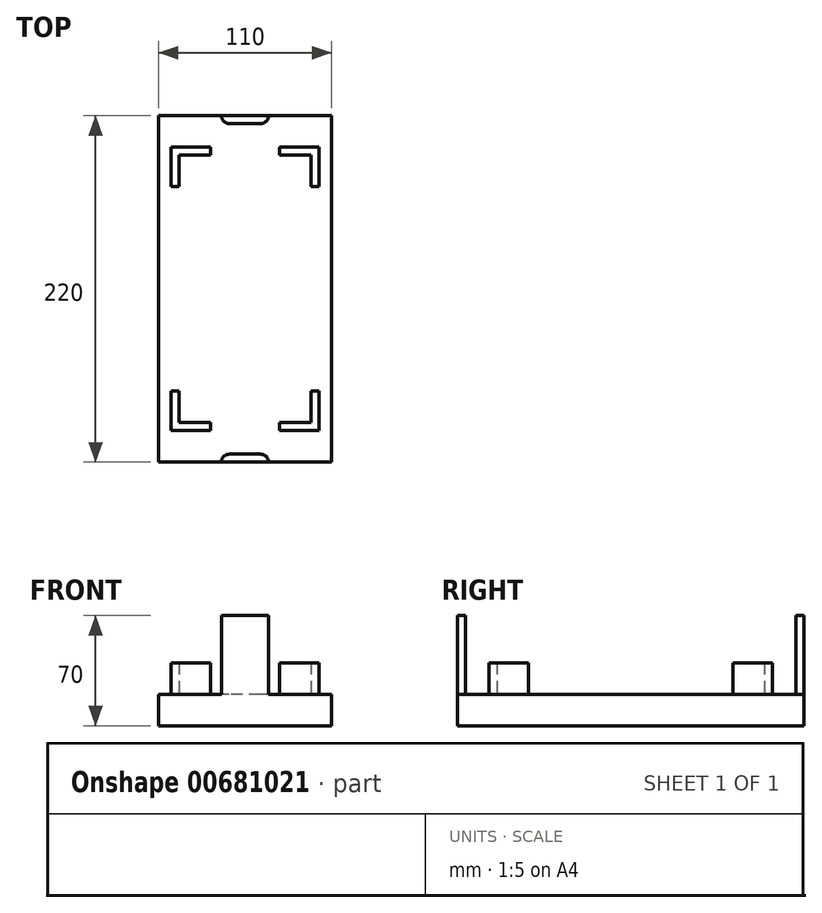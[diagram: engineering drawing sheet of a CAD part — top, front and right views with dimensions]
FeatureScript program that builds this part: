
annotation { "Feature Type Name" : "Feature", "Feature Type Description" : "" }
export const myFeature = defineFeature(function(context is Context, id is Id, definition is map)
    precondition{}
    {
        {
            var Q0;
            Q0=qCreatedBy(makeId("Top.planeOp"),FACE);
            var sketch = newSketch(context, id + "F0", { "sketchPlane" : qUnion([Q0])});
            skLineSegment(sketch, "E0.bottom", {"start": v(0, 0) * mm, "end": v(110, 0) * mm});
            skLineSegment(sketch, "E0.top", {"start": v(0, -220) * mm, "end": v(110, -220) * mm});
            skLineSegment(sketch, "E0.left", {"start": v(0, 0) * mm, "end": v(0, -220) * mm});
            skLineSegment(sketch, "E0.right", {"start": v(110, 0) * mm, "end": v(110, -220) * mm});
            skSolve(sketch);
        }
        {
            var Q0;
            Q0 = qSketchRegion(id + "F0", true);
            extrude(context, id + "F1", {"entities" : qUnion([Q0]), "depth" : 20 * mm, "offsetDistance" : 25.4 * mm});
        }
        {
            var Q0;
            Q0=makeQuery(id+"F1.opExtrude","CAP_FACE",FACE,{"disambiguationData":[OSD([sQuery(id+"F0.wireOp",EDGE,"E0.bottom"),sQuery(id+"F0.wireOp",EDGE,"E0.top"),sQuery(id+"F0.wireOp",EDGE,"E0.left"),sQuery(id+"F0.wireOp",EDGE,"E0.right")])],"isStart":false});
            var sketch = newSketch(context, id + "F2", { "sketchPlane" : qUnion([Q0])});
            skLineSegment(sketch, "E1", {"start": v(8, -45) * mm, "end": v(8, -20) * mm});
            skLineSegment(sketch, "E2", {"start": v(8, -20) * mm, "end": v(33, -20) * mm});
            skLineSegment(sketch, "E3", {"start": v(33, -20) * mm, "end": v(33, -25) * mm});
            skLineSegment(sketch, "E4", {"start": v(33, -25) * mm, "end": v(13, -25) * mm});
            skLineSegment(sketch, "E5", {"start": v(13, -25) * mm, "end": v(13, -45) * mm});
            skLineSegment(sketch, "E6", {"start": v(13, -45) * mm, "end": v(8, -45) * mm});
            skLineSegment(sketch, "E7", {"start": v(-31.27, -110) * mm, "end": v(131.1, -110) * mm, "construction": true});
            skLineSegment(sketch, "E8", {"start": v(55, 8.14) * mm, "end": v(55, -298.1) * mm, "construction": true});
            skLineSegment(sketch, "E9.MirrorCS", {"start": v(55, -58.14) * mm, "end": v(55, 248.1) * mm, "construction": true});
            skLineSegment(sketch, "E10.MirrorCS", {"start": v(77, -25) * mm, "end": v(97, -25) * mm});
            skLineSegment(sketch, "E11.MirrorCS", {"start": v(102, -20) * mm, "end": v(77, -20) * mm});
            skLineSegment(sketch, "E12.MirrorCS", {"start": v(77, -20) * mm, "end": v(77, -25) * mm});
            skLineSegment(sketch, "E13.MirrorCS", {"start": v(102, -45) * mm, "end": v(102, -20) * mm});
            skLineSegment(sketch, "E14.MirrorCS", {"start": v(97, -45) * mm, "end": v(102, -45) * mm});
            skLineSegment(sketch, "E15.MirrorCS", {"start": v(97, -25) * mm, "end": v(97, -45) * mm});
            skLineSegment(sketch, "E16.MirrorCS", {"start": v(33, -195) * mm, "end": v(13, -195) * mm});
            skLineSegment(sketch, "E17.MirrorCS", {"start": v(8, -200) * mm, "end": v(33, -200) * mm});
            skLineSegment(sketch, "E18.MirrorCS", {"start": v(33, -200) * mm, "end": v(33, -195) * mm});
            skLineSegment(sketch, "E19.MirrorCS", {"start": v(8, -175) * mm, "end": v(8, -200) * mm});
            skLineSegment(sketch, "E20.MirrorCS", {"start": v(13, -175) * mm, "end": v(8, -175) * mm});
            skLineSegment(sketch, "E21.MirrorCS", {"start": v(13, -195) * mm, "end": v(13, -175) * mm});
            skLineSegment(sketch, "E22.MirrorCS", {"start": v(97, -195) * mm, "end": v(97, -175) * mm});
            skLineSegment(sketch, "E23.MirrorCS", {"start": v(77, -195) * mm, "end": v(97, -195) * mm});
            skLineSegment(sketch, "E24.MirrorCS", {"start": v(102, -200) * mm, "end": v(77, -200) * mm});
            skLineSegment(sketch, "E25.MirrorCS", {"start": v(97, -175) * mm, "end": v(102, -175) * mm});
            skLineSegment(sketch, "E26.MirrorCS", {"start": v(102, -175) * mm, "end": v(102, -200) * mm});
            skLineSegment(sketch, "E27.MirrorCS", {"start": v(77, -200) * mm, "end": v(77, -195) * mm});
            skSolve(sketch);
        }
        {
            var Q0;
            Q0 = qSketchRegion(id + "F2", true);
            extrude(context, id + "F3", {"entities" : qUnion([Q0]), "operationType" : NewBodyOperationType.ADD, "depth" : 20 * mm, "offsetDistance" : 25 * mm});
        }
        {
            var Q0;
            Q0=makeQuery(id+"F1.opExtrude","CAP_FACE",FACE,{"disambiguationData":[OSD([sQuery(id+"F0.wireOp",EDGE,"E0.bottom"),sQuery(id+"F0.wireOp",EDGE,"E0.top"),sQuery(id+"F0.wireOp",EDGE,"E0.left"),sQuery(id+"F0.wireOp",EDGE,"E0.right")])],"isStart":false});
            var sketch = newSketch(context, id + "F4", { "sketchPlane" : qUnion([Q0])});
            skLineSegment(sketch, "E28.bottom", {"start": v(70, 0) * mm, "end": v(40, 0) * mm});
            skLineSegment(sketch, "E28.top", {"start": v(70, -5) * mm, "end": v(40, -5) * mm});
            skLineSegment(sketch, "E28.left", {"start": v(70, 0) * mm, "end": v(70, -5) * mm});
            skLineSegment(sketch, "E28.right", {"start": v(40, 0) * mm, "end": v(40, -5) * mm});
            skLineSegment(sketch, "E29", {"start": v(122.77, -110) * mm, "end": v(12.89, -110) * mm, "construction": true});
            skLineSegment(sketch, "E30.MirrorCS", {"start": v(70, -215) * mm, "end": v(40, -215) * mm});
            skLineSegment(sketch, "E31.MirrorCS", {"start": v(70, -220) * mm, "end": v(40, -220) * mm});
            skLineSegment(sketch, "E32.MirrorCS", {"start": v(40, -220) * mm, "end": v(40, -215) * mm});
            skLineSegment(sketch, "E33.MirrorCS", {"start": v(70, -220) * mm, "end": v(70, -215) * mm});
            skSolve(sketch);
        }
        {
            var Q0;
            Q0 = qSketchRegion(id + "F4", true);
            extrude(context, id + "F5", {"entities" : qUnion([Q0]), "operationType" : NewBodyOperationType.ADD, "depth" : 50 * mm, "offsetDistance" : 25 * mm});
        }
        {
            var Q0;
            Q0=makeQuery(id+"F5.opExtrude","SWEPT_EDGE",EDGE,{"disambiguationData":[OSD([sQuery(id+"F4.wireOp",EDGE,"E28.top"),sQuery(id+"F4.wireOp",EDGE,"E28.right")])]});
            var Q1;
            Q1=makeQuery(id+"F5.opExtrude","SWEPT_EDGE",EDGE,{"disambiguationData":[OSD([sQuery(id+"F4.wireOp",EDGE,"E28.top"),sQuery(id+"F4.wireOp",EDGE,"E28.left")])]});
            var Q2;
            Q2=makeQuery(id+"F5.opExtrude","SWEPT_EDGE",EDGE,{"disambiguationData":[OSD([sQuery(id+"F4.wireOp",EDGE,"E30.MirrorCS"),sQuery(id+"F4.wireOp",EDGE,"E32.MirrorCS")])]});
            var Q3;
            Q3=makeQuery(id+"F5.opExtrude","SWEPT_EDGE",EDGE,{"disambiguationData":[OSD([sQuery(id+"F4.wireOp",EDGE,"E30.MirrorCS"),sQuery(id+"F4.wireOp",EDGE,"E33.MirrorCS")])]});
            fillet(context, id + "F6", {"entities" : qUnion([Q0, Q1, Q2, Q3]), "radius" : 5 * mm, "tangentPropagation" : true, "allowEdgeOverflow" : false});
        }
    });
